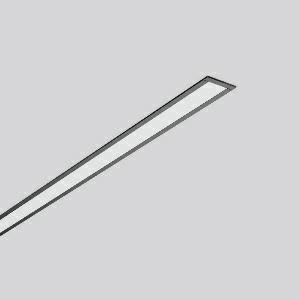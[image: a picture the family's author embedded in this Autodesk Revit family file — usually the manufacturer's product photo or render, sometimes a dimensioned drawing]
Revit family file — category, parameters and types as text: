
# Revit family: less_is_more_27_312176_003_1_03a4
name_source: partatom
category: Lighting Fixtures
units: mm (PartAtom-declared; Revit-internal decimal feet)

## family parameters
Cut with Voids When Loaded = No
Host = Face
Light Source = No
Part Type = Normal
Room Calculation Point = No
Round Connector Dimension = Use Diameter
Shared = No

## types (1)
- LESS IS MORE 27 (1 x LED Modul 840, 1600 lm, 4000)
    Apparent Load = 25 VA
    CIE Flux Codes = 48 79 96 100 100
    Color Rendering = 80
    Color Temperature = 4000
    Default Elevation = 1800 mm
    Description = Series: LESS IS MORE 27
Recessed ceiling and wall luminaire with slim design. Housing: extruded aluminium profile, powder-coated. End cap aluminium powder-coated. Diffuser made of non-yellowing plastic (PMMA), opal. Suitable for Recessed ceiling mounting, wall (recessed). External driver with connecting cable. 
Colour: deep black, matt (RAL 9005)
Length: 1014 mm
Width: 38 mm
Height: 2 mm
Cut-out length: 1006 mm
Cut-out width: 30 mm
Recess height: 45-60 mm
Luminaire: recess height: 37 mm
Lamp: LED
Socket: without socket
Colour temperature: 4000K
Colour rendering index (CRI): 82
System power: 25 W
Rated luminous flux: 1600 lm
Luminous efficiency: 64 lm/W
Control gear: Regulated power supply
Protection class: II
Type of protection: IP 20
    Height = 0 mm  [stored 0 ft]
    Lamp = 1 x LED Modul 840
    Lamp Light Flux = 1600 lm
    Lamp count = 1
    Length = 1014 mm
    Lifetime = 50000 h
    Luminous efficacy = 64 lm/W
    Manufacturer = RZB
    ModVariant = No
    Model = 312176.003.1
    Mounting Place = Ceiling, Wall
    Mounting Type = Recessed
    Number of Poles = 1
    OnlyDefault = Yes
    Power Factor = 1
    Product Name = LESS IS MORE 27
    Product group = Recessed LED linear luminaires
    ProductGroupID = 407
    Protection Class = Protection class II
    Protection Degree = IP 20
    RLX_Detail_Level = 1
    RLX_Emergency_Light_Flux = 0 lm
    RLX_Emergency_Type = 0
    RLX_Emergency_Type_DB = No
    RlxData = <blob elided: 26149 chars, md5=b29a1bd0>
    Socket = socket
    Standby Power = 0 W
    System Light Flux = 1600 lm
    System Power = 25 W
    Type Comments = Product without accessories
    Type Image = 312176.003.jpg
    URL = http://relux.com
    VarID = ---
    Voltage = 230 V
    Voltage Range = 220-240 V
    Weight = 0.00 kg
    Width = 38 mm

note: [stored X ft] marks values corroborated as IEEE doubles in the binary element streams (Revit-internal decimal feet)

## geometry (parser evidence)
native form markers: Blend x4, Sweep x12
no freeform markers — native parametric forms only
